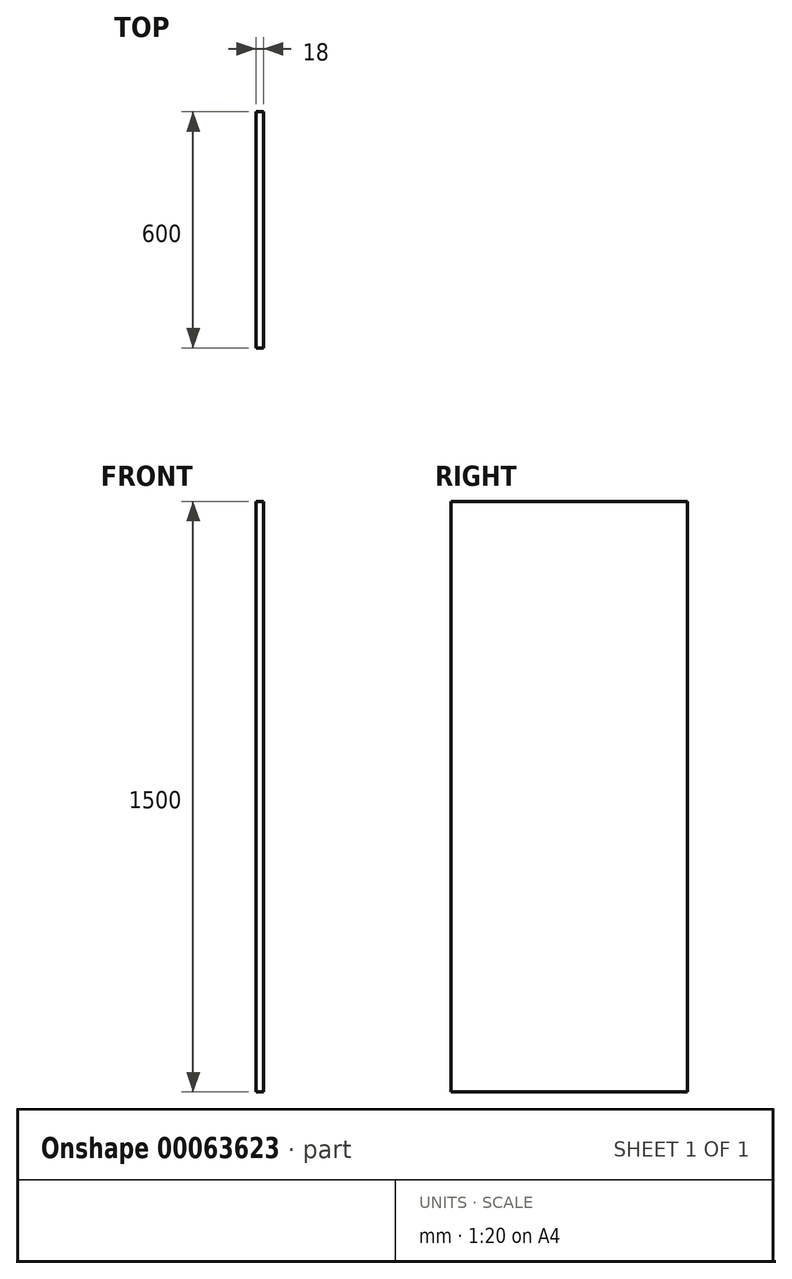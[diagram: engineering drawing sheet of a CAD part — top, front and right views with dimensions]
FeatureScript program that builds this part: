
annotation { "Feature Type Name" : "Feature", "Feature Type Description" : "" }
export const myFeature = defineFeature(function(context is Context, id is Id, definition is map)
    precondition{}
    {
        {
            var Q0;
            Q0=qCreatedBy(makeId("Right.planeOp"),FACE);
            var sketch = newSketch(context, id + "F0", { "sketchPlane" : qUnion([Q0])});
            skLineSegment(sketch, "E0.bottom", {"start": v(0, 0) * mm, "end": v(600, 0) * mm});
            skLineSegment(sketch, "E0.top", {"start": v(0, -1500) * mm, "end": v(600, -1500) * mm});
            skLineSegment(sketch, "E0.left", {"start": v(0, 0) * mm, "end": v(0, -1500) * mm});
            skLineSegment(sketch, "E0.right", {"start": v(600, 0) * mm, "end": v(600, -1500) * mm});
            skSolve(sketch);
        }
        {
            var Q0;
            Q0=makeQuery(id+"F0.imprint","IMPRINT",FACE,{"disambiguationData":[TD([[makeQuery(id+"F0.imprint","IMPRINT",EDGE,{"derivedFrom":sQuery(id+"F0.wireOp",EDGE,"E0.bottom")}),-1.0]])]});
            extrude(context, id + "F1", {"entities" : qUnion([Q0]), "depth" : 18 * mm});
        }
    });
